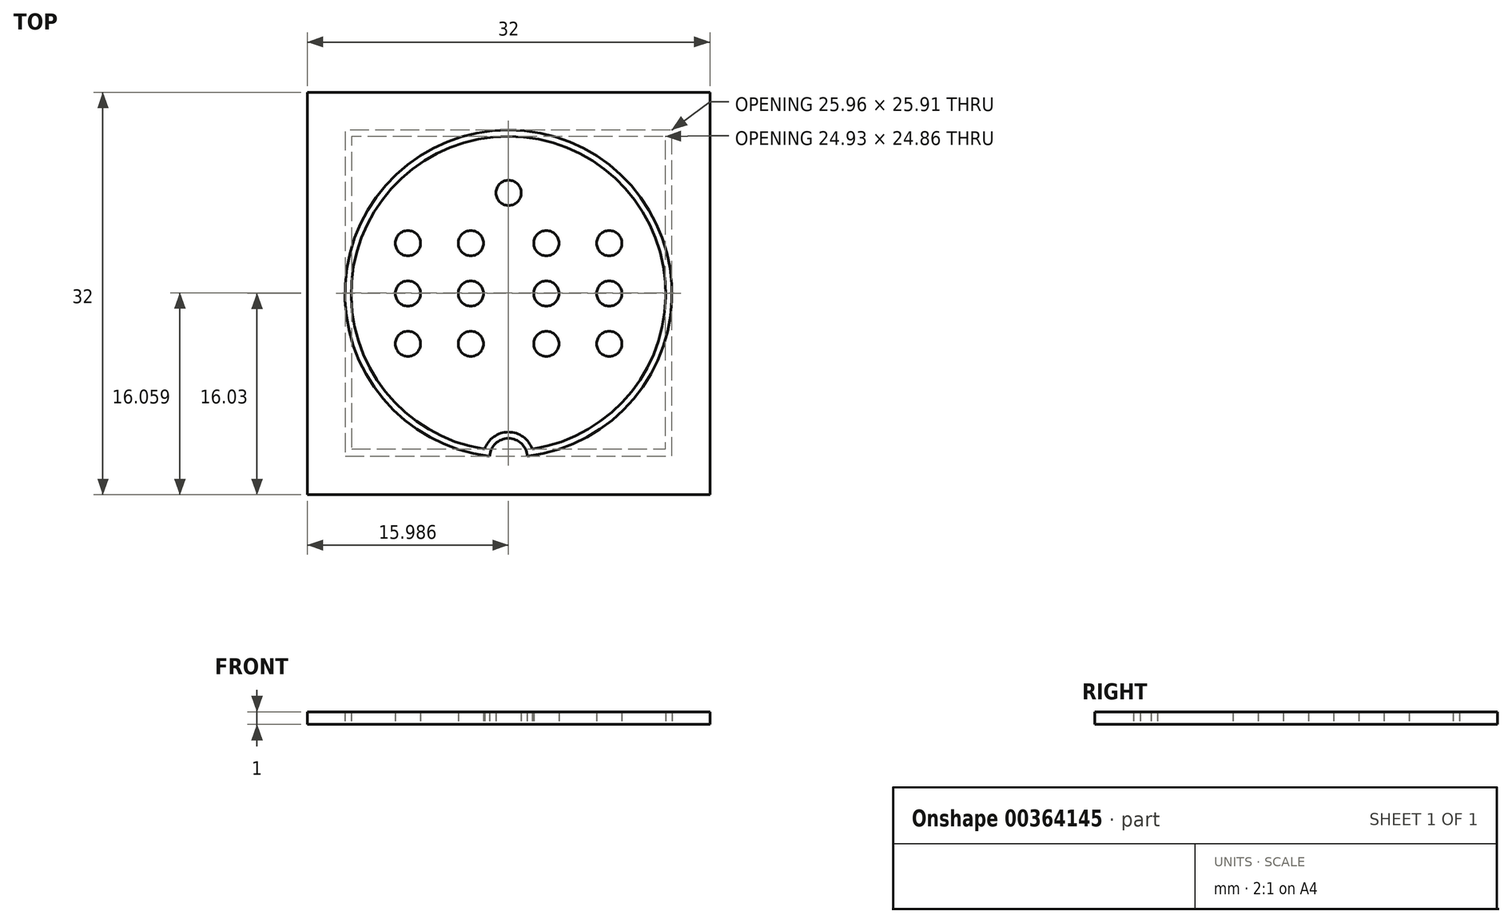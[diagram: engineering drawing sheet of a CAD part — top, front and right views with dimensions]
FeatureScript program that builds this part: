
annotation { "Feature Type Name" : "Feature", "Feature Type Description" : "" }
export const myFeature = defineFeature(function(context is Context, id is Id, definition is map)
    precondition{}
    {
        {
            var Q0;
            Q0=qCreatedBy(makeId("Top.planeOp"),FACE);
            var sketch = newSketch(context, id + "F0", { "sketchPlane" : qUnion([Q0])});
            skArc(sketch, "E0", {"start": v(1.88, -12.37) * mm, "mid": v(-0.01, 12.49) * mm, "end": v(-1.9, -12.37) * mm});
            skLineSegment(sketch, "E1", {"start": v(-0.01, -0.01) * mm, "end": v(0, 0) * mm});
            skArc(sketch, "E2", {"start": v(1.48, -12.93) * mm, "mid": v(-0.01, 12.99) * mm, "end": v(-1.51, -12.93) * mm});
            skArc(sketch, "E3", {"start": v(1.48, -12.93) * mm, "mid": v(-0.01, -11.51) * mm, "end": v(-1.51, -12.93) * mm});
            skArc(sketch, "E4", {"start": v(1.88, -12.37) * mm, "mid": v(-0.01, -11.01) * mm, "end": v(-1.9, -12.37) * mm});
            skLineSegment(sketch, "E5.bottom", {"start": v(16, -16) * mm, "end": v(-16, -16) * mm});
            skLineSegment(sketch, "E5.top", {"start": v(16, 16) * mm, "end": v(-16, 16) * mm});
            skLineSegment(sketch, "E5.left", {"start": v(16, -16) * mm, "end": v(16, 16) * mm});
            skLineSegment(sketch, "E5.right", {"start": v(-16, -16) * mm, "end": v(-16, 16) * mm});
            skPoint(sketch, "E5.middle", {"position": v(0, 0) * mm});
            skCircle(sketch, "E6", {"center": v(3, 4) * mm, "radius": 1 * mm});
            skCircle(sketch, "E7", {"center": v(8, 4) * mm, "radius": 1 * mm});
            skCircle(sketch, "E8", {"center": v(-3, 4) * mm, "radius": 1 * mm});
            skCircle(sketch, "E9", {"center": v(-8, 4) * mm, "radius": 1 * mm});
            skCircle(sketch, "E10", {"center": v(-8, 0) * mm, "radius": 1 * mm});
            skCircle(sketch, "E11", {"center": v(-8, -4) * mm, "radius": 1 * mm});
            skCircle(sketch, "E12", {"center": v(-3, 0) * mm, "radius": 1 * mm});
            skCircle(sketch, "E13", {"center": v(-3, -4) * mm, "radius": 1 * mm});
            skCircle(sketch, "E14", {"center": v(3, 0) * mm, "radius": 1 * mm});
            skCircle(sketch, "E15", {"center": v(8, 0) * mm, "radius": 1 * mm});
            skCircle(sketch, "E16", {"center": v(3, -4) * mm, "radius": 1 * mm});
            skCircle(sketch, "E17", {"center": v(8, -4) * mm, "radius": 1 * mm});
            skCircle(sketch, "E18", {"center": v(0, 8) * mm, "radius": 1 * mm});
            skSolve(sketch);
        }
        {
            var Q0;
            Q0=makeQuery(id+"F0.imprint","IMPRINT",FACE,{"disambiguationData":[TD([[makeQuery(id+"F0.imprint","IMPRINT",EDGE,{"derivedFrom":sQuery(id+"F0.wireOp",EDGE,"E2")}),1.0]])]});
            var Q1;
            Q1=makeQuery(id+"F0.imprint","IMPRINT",FACE,{"disambiguationData":[TD([[makeQuery(id+"F0.imprint","IMPRINT",EDGE,{"derivedFrom":sQuery(id+"F0.wireOp",EDGE,"d27943b6-2914-40e9-a132-a8c85ac11e38")}),1.0]])]});
            var Q2;
            Q2=makeQuery(id+"F0.imprint","IMPRINT",FACE,{"disambiguationData":[TD([[makeQuery(id+"F0.imprint","IMPRINT",EDGE,{"derivedFrom":sQuery(id+"F0.wireOp",EDGE,"8f6016f4-f1cb-480f-b7be-917d0405e12e")}),1.0]])]});
            var Q3;
            Q3=makeQuery(id+"F0.imprint","IMPRINT",FACE,{"disambiguationData":[TD([[makeQuery(id+"F0.imprint","IMPRINT",EDGE,{"derivedFrom":sQuery(id+"F0.wireOp",EDGE,"7b6a4aa2-640f-4422-b75e-bf37a9b54871")}),1.0]])]});
            var Q4;
            Q4=makeQuery(id+"F0.imprint","IMPRINT",FACE,{"disambiguationData":[TD([[makeQuery(id+"F0.imprint","IMPRINT",EDGE,{"derivedFrom":sQuery(id+"F0.wireOp",EDGE,"EjpMIuij-bMRM-TPGo-DypF-psRe76QZ1od6")}),1.0]])]});
            var Q5;
            Q5=makeQuery(id+"F0.imprint","IMPRINT",FACE,{"disambiguationData":[TD([[makeQuery(id+"F0.imprint","IMPRINT",EDGE,{"derivedFrom":sQuery(id+"F0.wireOp",EDGE,"045fe6e6-b52b-4188-822a-6cd7bc594825")}),1.0]])]});
            var Q6;
            Q6=makeQuery(id+"F0.imprint","IMPRINT",FACE,{"disambiguationData":[TD([[makeQuery(id+"F0.imprint","IMPRINT",EDGE,{"derivedFrom":sQuery(id+"F0.wireOp",EDGE,"174910c9-1013-46cf-ba4d-a46a06b0ce87")}),1.0]])]});
            var Q7;
            Q7=makeQuery(id+"F0.imprint","IMPRINT",FACE,{"disambiguationData":[TD([[makeQuery(id+"F0.imprint","IMPRINT",EDGE,{"derivedFrom":sQuery(id+"F0.wireOp",EDGE,"445c56d2-9f28-4655-9398-6fe16b3b1b2e")}),1.0]])]});
            var Q8;
            Q8=makeQuery(id+"F0.imprint","IMPRINT",FACE,{"disambiguationData":[TD([[makeQuery(id+"F0.imprint","IMPRINT",EDGE,{"derivedFrom":sQuery(id+"F0.wireOp",EDGE,"f9b22722-50a5-4e01-aecb-2c5de581573f")}),1.0]])]});
            var Q9;
            Q9=makeQuery(id+"F0.imprint","IMPRINT",FACE,{"disambiguationData":[TD([[makeQuery(id+"F0.imprint","IMPRINT",EDGE,{"derivedFrom":sQuery(id+"F0.wireOp",EDGE,"ztm3Eoz2-73oX-c2Fz-zSjY-5273HLMfsEtm")}),1.0]])]});
            var Q10;
            Q10=makeQuery(id+"F0.imprint","IMPRINT",FACE,{"disambiguationData":[TD([[makeQuery(id+"F0.imprint","IMPRINT",EDGE,{"derivedFrom":sQuery(id+"F0.wireOp",EDGE,"E9")}),1.0]])]});
            var Q11;
            Q11=makeQuery(id+"F0.imprint","IMPRINT",FACE,{"disambiguationData":[TD([[makeQuery(id+"F0.imprint","IMPRINT",EDGE,{"derivedFrom":sQuery(id+"F0.wireOp",EDGE,"E8")}),1.0]])]});
            var Q12;
            Q12=makeQuery(id+"F0.imprint","IMPRINT",FACE,{"disambiguationData":[TD([[makeQuery(id+"F0.imprint","IMPRINT",EDGE,{"derivedFrom":sQuery(id+"F0.wireOp",EDGE,"E18")}),1.0]])]});
            var Q13;
            Q13=makeQuery(id+"F0.imprint","IMPRINT",FACE,{"disambiguationData":[TD([[makeQuery(id+"F0.imprint","IMPRINT",EDGE,{"derivedFrom":sQuery(id+"F0.wireOp",EDGE,"E6")}),1.0]])]});
            var Q14;
            Q14=makeQuery(id+"F0.imprint","IMPRINT",FACE,{"disambiguationData":[TD([[makeQuery(id+"F0.imprint","IMPRINT",EDGE,{"derivedFrom":sQuery(id+"F0.wireOp",EDGE,"E7")}),1.0]])]});
            var Q15;
            Q15=makeQuery(id+"F0.imprint","IMPRINT",FACE,{"disambiguationData":[TD([[makeQuery(id+"F0.imprint","IMPRINT",EDGE,{"derivedFrom":sQuery(id+"F0.wireOp",EDGE,"E15")}),1.0]])]});
            var Q16;
            Q16=makeQuery(id+"F0.imprint","IMPRINT",FACE,{"disambiguationData":[TD([[makeQuery(id+"F0.imprint","IMPRINT",EDGE,{"derivedFrom":sQuery(id+"F0.wireOp",EDGE,"E17")}),1.0]])]});
            var Q17;
            Q17=makeQuery(id+"F0.imprint","IMPRINT",FACE,{"disambiguationData":[TD([[makeQuery(id+"F0.imprint","IMPRINT",EDGE,{"derivedFrom":sQuery(id+"F0.wireOp",EDGE,"E16")}),1.0]])]});
            var Q18;
            Q18=makeQuery(id+"F0.imprint","IMPRINT",FACE,{"disambiguationData":[TD([[makeQuery(id+"F0.imprint","IMPRINT",EDGE,{"derivedFrom":sQuery(id+"F0.wireOp",EDGE,"E14")}),1.0]])]});
            var Q19;
            Q19=makeQuery(id+"F0.imprint","IMPRINT",FACE,{"disambiguationData":[TD([[makeQuery(id+"F0.imprint","IMPRINT",EDGE,{"derivedFrom":sQuery(id+"F0.wireOp",EDGE,"E12")}),1.0]])]});
            var Q20;
            Q20=makeQuery(id+"F0.imprint","IMPRINT",FACE,{"disambiguationData":[TD([[makeQuery(id+"F0.imprint","IMPRINT",EDGE,{"derivedFrom":sQuery(id+"F0.wireOp",EDGE,"E13")}),1.0]])]});
            var Q21;
            Q21=makeQuery(id+"F0.imprint","IMPRINT",FACE,{"disambiguationData":[TD([[makeQuery(id+"F0.imprint","IMPRINT",EDGE,{"derivedFrom":sQuery(id+"F0.wireOp",EDGE,"E11")}),1.0]])]});
            var Q22;
            Q22=makeQuery(id+"F0.imprint","IMPRINT",FACE,{"disambiguationData":[TD([[makeQuery(id+"F0.imprint","IMPRINT",EDGE,{"derivedFrom":sQuery(id+"F0.wireOp",EDGE,"E10")}),1.0]])]});
            extrude(context, id + "F1", {"entities" : qUnion([Q0, Q1, Q2, Q3, Q4, Q5, Q6, Q7, Q8, Q9, Q10, Q11, Q12, Q13, Q14, Q15, Q16, Q17, Q18, Q19, Q20, Q21, Q22]), "depth" : 1 * mm});
        }
        {
            var Q0;
            Q0=makeQuery(id+"F0.imprint","IMPRINT",FACE,{"disambiguationData":[TD([[makeQuery(id+"F0.imprint","IMPRINT",EDGE,{"derivedFrom":sQuery(id+"F0.wireOp",EDGE,"E2")}),-1.0]])]});
            extrude(context, id + "F2", {"entities" : qUnion([Q0]), "depth" : 1 * mm});
        }
    });
